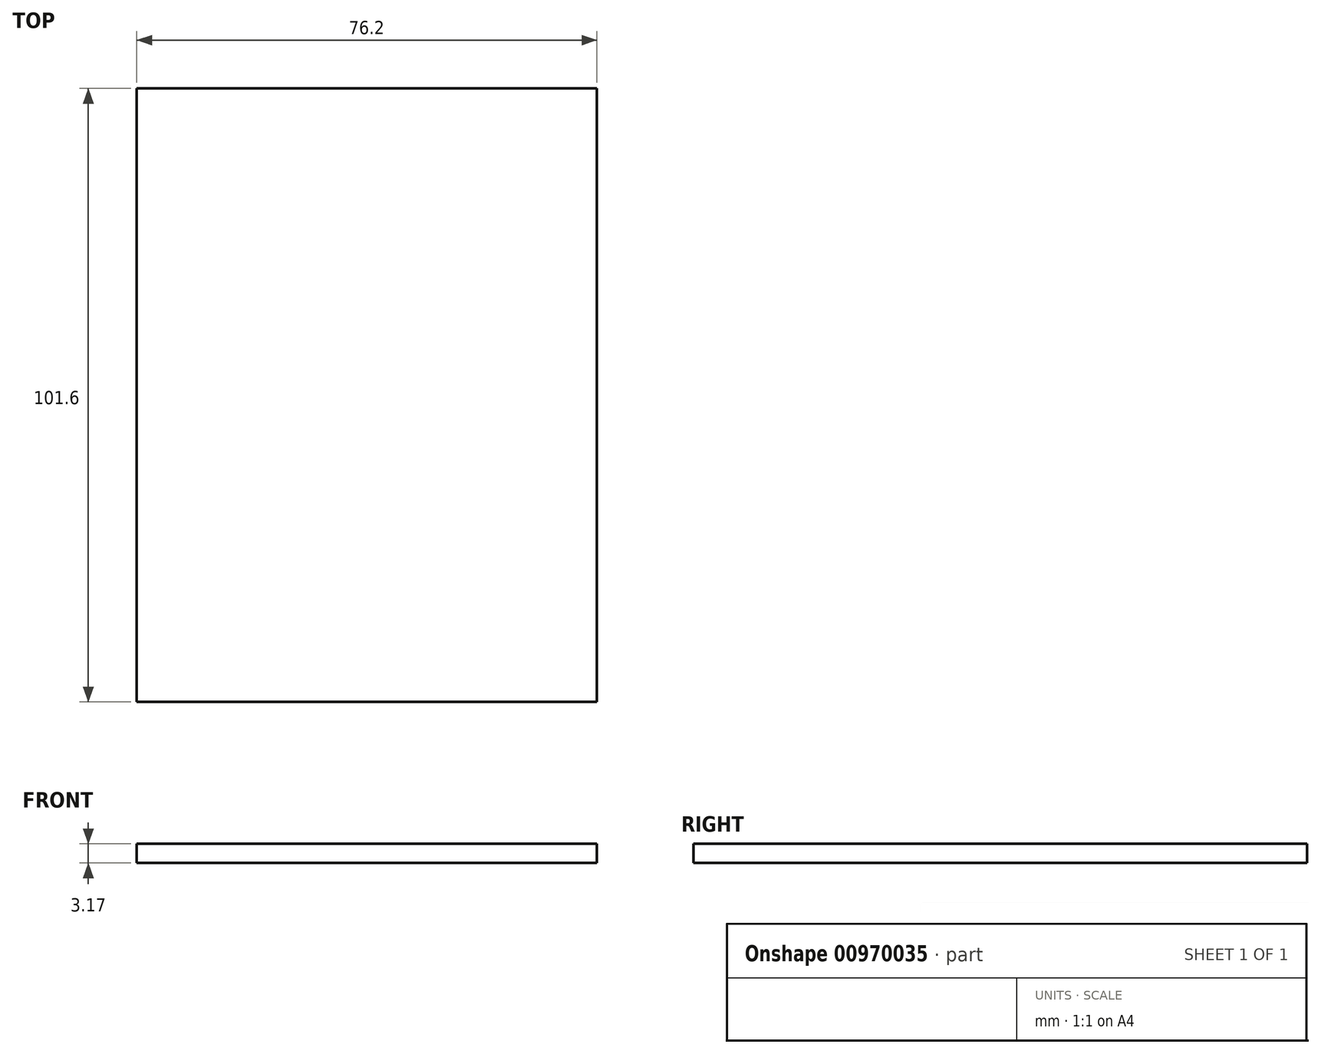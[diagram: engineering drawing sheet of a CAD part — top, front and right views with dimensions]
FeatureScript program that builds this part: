
annotation { "Feature Type Name" : "Feature", "Feature Type Description" : "" }
export const myFeature = defineFeature(function(context is Context, id is Id, definition is map)
    precondition{}
    {
        {
            var Q0;
            Q0=qCreatedBy(makeId("Top.planeOp"),FACE);
            var sketch = newSketch(context, id + "F0", { "sketchPlane" : qUnion([Q0])});
            skLineSegment(sketch, "E0.bottom", {"start": v(0, 0) * mm, "end": v(76.2, 0) * mm});
            skLineSegment(sketch, "E0.top", {"start": v(0, 101.6) * mm, "end": v(76.2, 101.6) * mm});
            skLineSegment(sketch, "E0.left", {"start": v(0, 0) * mm, "end": v(0, 101.6) * mm});
            skLineSegment(sketch, "E0.right", {"start": v(76.2, 0) * mm, "end": v(76.2, 101.6) * mm});
            skSolve(sketch);
        }
        {
            var Q0;
            Q0=makeQuery(id+"F0.imprint","IMPRINT",FACE,{"disambiguationData":[TD([[makeQuery(id+"F0.imprint","IMPRINT",EDGE,{"derivedFrom":sQuery(id+"F0.wireOp",EDGE,"E0.bottom")}),1.0]])]});
            extrude(context, id + "F1", {"entities" : qUnion([Q0]), "depth" : 3.17 * mm, "offsetDistance" : 25.4 * mm});
        }
    });
